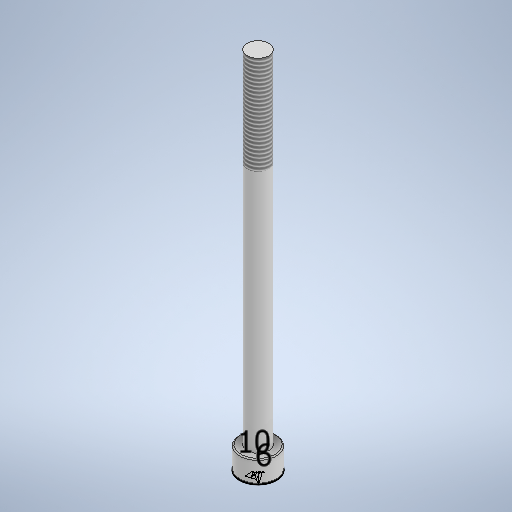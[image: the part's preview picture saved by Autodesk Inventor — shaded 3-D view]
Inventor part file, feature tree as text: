
AUTODESK INVENTOR PART (.ipt)
format: ipt  version: 2025 (Build 290162000, 162)  size: 275,968 bytes
history: native  units: mm
features: extrude x3, sketch x2, fillet x2, thread x1
ambient origin geometry x8: Origin, YZ Plane, XZ Plane, XY Plane, X Axis, Y Axis, Z Axis, Center Point
bodies: Solid1 (feature_tree)
feature tree (8):
  sketch  "Sketch1"  dims[d0=10.0mm d1=6.0mm]
  extrude  "Extrusion1"  Depth=6.0mm
  extrude  "Extrusion2"  Depth=6.0mm TaperAngle=0.0deg
  fillet  "Fillet1"  Radius=0.3mm
  fillet  "Fillet2"  Radius=0.3mm
  extrude  "Extrusion3"  Depth=5.0mm
  thread  "Thread1"  [1 undecoded]
  sketch  "Sketch2"  dims[d2=100.0mm d3=0.0mm d4=6.0mm d5=0.0mm d6=0.3mm d7=0.3mm d8=5.0mm d9=1.3mm d10=0.0mm d11=27.0mm d12=0.0mm]
note: 1 required parameter value undecoded (feature->parameter linkage not recoverable at this tier; creation-order binding heuristic only, values carry confidence <= 0.55)
